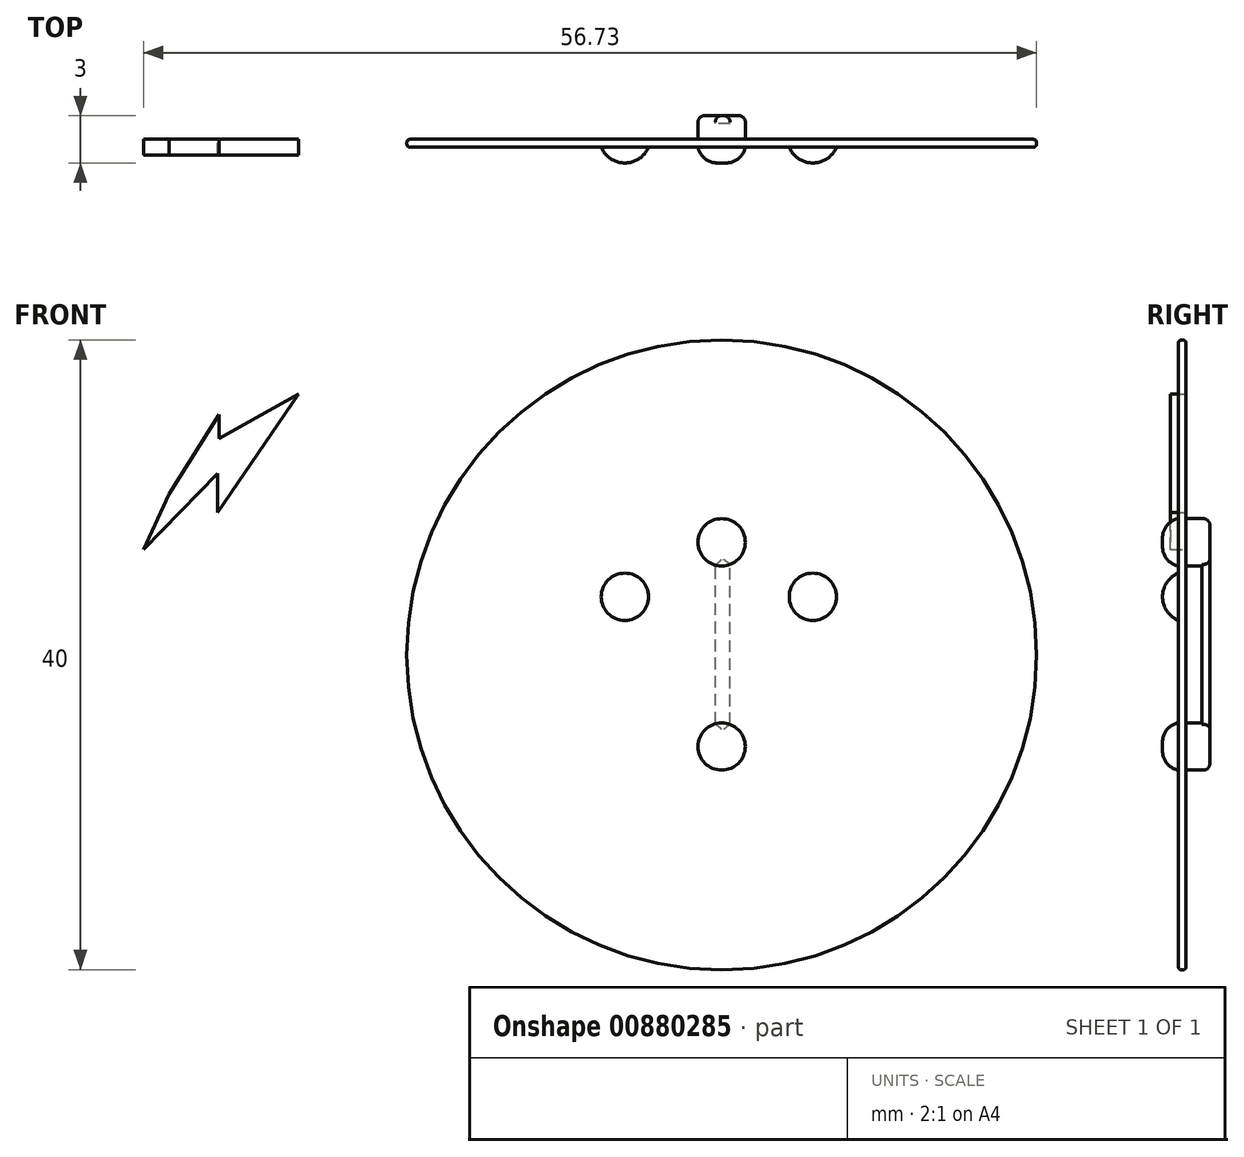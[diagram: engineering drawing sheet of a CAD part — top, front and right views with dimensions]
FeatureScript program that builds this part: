
annotation { "Feature Type Name" : "Feature", "Feature Type Description" : "" }
export const myFeature = defineFeature(function(context is Context, id is Id, definition is map)
    precondition{}
    {
        {
            var Q0;
            Q0=qCreatedBy(makeId("Front.planeOp"),FACE);
            var sketch = newSketch(context, id + "F0", { "sketchPlane" : qUnion([Q0])});
            skCircle(sketch, "E0", {"center": v(0, 0) * mm, "radius": 20 * mm});
            skSolve(sketch);
        }
        {
            var Q0;
            Q0=makeQuery(id+"F0.imprint","IMPRINT",FACE,{"disambiguationData":[TD([[makeQuery(id+"F0.imprint","IMPRINT",EDGE,{"derivedFrom":sQuery(id+"F0.wireOp",EDGE,"E0")}),1.0]])]});
            extrude(context, id + "F1", {"entities" : qUnion([Q0]), "depth" : .5 * mm, "offsetDistance" : 25 * mm});
        }
        {
            var Q0;
            Q0=makeQuery(id+"F1.opExtrude","CAP_FACE",FACE,{"disambiguationData":[OSD([sQuery(id+"F0.wireOp",EDGE,"E0")])],"isStart":true});
            var Q1;
            Q1=makeQuery(id+"F1.opExtrude","CAP_EDGE",EDGE,{"disambiguationData":[OSD([sQuery(id+"F0.wireOp",EDGE,"E0")])],"isStart":true});
            var Q2;
            Q2=makeQuery(id+"F1.opExtrude","CAP_EDGE",EDGE,{"disambiguationData":[OSD([sQuery(id+"F0.wireOp",EDGE,"E0")])],"isStart":false});
            var Q3;
            Q3=makeQuery(id+"F1.opExtrude","CAP_FACE",FACE,{"disambiguationData":[OSD([sQuery(id+"F0.wireOp",EDGE,"E0")])],"isStart":false});
            fillet(context, id + "F2", {"entities" : qUnion([Q0, Q1, Q2, Q3]), "radius" : .2 * mm, "tangentPropagation" : true, "allowEdgeOverflow" : false});
        }
        {
            var Q0;
            Q0=qCreatedBy(makeId("Front.planeOp"),FACE);
            var sketch = newSketch(context, id + "F3", { "sketchPlane" : qUnion([Q0])});
            skCircle(sketch, "E1", {"center": v(0, 7.16) * mm, "radius": 1.5 * mm});
            skCircle(sketch, "E2", {"center": v(0, -5.82) * mm, "radius": 1.5 * mm});
            skSolve(sketch);
        }
        {
            var Q0;
            Q0=makeQuery(id+"F3.imprint","IMPRINT",FACE,{"disambiguationData":[TD([[makeQuery(id+"F3.imprint","IMPRINT",EDGE,{"derivedFrom":sQuery(id+"F3.wireOp",EDGE,"E2")}),1.0]])]});
            var Q1;
            Q1=makeQuery(id+"F3.imprint","IMPRINT",FACE,{"disambiguationData":[TD([[makeQuery(id+"F3.imprint","IMPRINT",EDGE,{"derivedFrom":sQuery(id+"F3.wireOp",EDGE,"E1")}),1.0]])]});
            extrude(context, id + "F4", {"entities" : qUnion([Q0, Q1]), "operationType" : NewBodyOperationType.ADD, "depth" : 1.5 * mm, "offsetDistance" : 25 * mm, "hasSecondDirection" : true, "secondDirectionOppositeDirection" : true, "secondDirectionDepth" : 1.5 * mm});
        }
        {
            var Q0;
            Q0=makeQuery(id+"F4.opExtrude","CAP_FACE",FACE,{"disambiguationData":[OSD([sQuery(id+"F3.wireOp",EDGE,"E2")])],"isStart":false});
            var Q1;
            Q1=makeQuery(id+"F4.opExtrude","CAP_FACE",FACE,{"disambiguationData":[OSD([sQuery(id+"F3.wireOp",EDGE,"E1")])],"isStart":false});
            fillet(context, id + "F5", {"entities" : qUnion([Q0, Q1]), "radius" : 1.23 * mm, "tangentPropagation" : true, "allowEdgeOverflow" : false});
        }
        {
            var Q0;
            Q0=makeQuery(id+"F4.opExtrude","CAP_FACE",FACE,{"disambiguationData":[OSD([sQuery(id+"F3.wireOp",EDGE,"E1")])],"isStart":true});
            var sketch = newSketch(context, id + "F6", { "sketchPlane" : qUnion([Q0])});
            skLineSegment(sketch, "E3.bottom", {"start": v(-0.54, -5.9) * mm, "end": v(0.4, -5.9) * mm});
            skLineSegment(sketch, "E3.top", {"start": v(-0.54, 7.33) * mm, "end": v(0.4, 7.33) * mm});
            skLineSegment(sketch, "E3.left", {"start": v(-0.54, -5.9) * mm, "end": v(-0.54, 7.33) * mm});
            skLineSegment(sketch, "E3.right", {"start": v(0.4, -5.9) * mm, "end": v(0.4, 7.33) * mm});
            skSolve(sketch);
        }
        {
            var Q0;
            {var subQ0=sQuery(id+"F6.wireOp",EDGE,"E3.bottom");Q0=makeQuery(id+"F6.imprint","IMPRINT",FACE,{"disambiguationData":[TD([[makeQuery(id+"F6.imprint","IMPRINT",EDGE,{"derivedFrom":subQ0}),1.0]])]});}
            var Q1;
            {var subQ0=sQuery(id+"F6.wireOp",EDGE,"E3.top");Q1=makeQuery(id+"F6.imprint","IMPRINT",FACE,{"disambiguationData":[TD([[makeQuery(id+"F6.imprint","IMPRINT",EDGE,{"derivedFrom":subQ0}),-1.0]])]});}
            extrude(context, id + "F7", {"entities" : qUnion([Q0, Q1]), "operationType" : NewBodyOperationType.ADD, "oppositeDirection" : true, "depth" : .5 * mm, "offsetDistance" : 25 * mm});
        }
        {
            var Q0;
            Q0=makeQuery(id+"F4.opExtrude","CAP_EDGE",EDGE,{"disambiguationData":[OSD([sQuery(id+"F3.wireOp",EDGE,"E1")])],"isStart":true});
            var Q1;
            Q1=makeQuery(id+"F7.opExtrude","CAP_EDGE",EDGE,{"disambiguationData":[OSD([sQuery(id+"F6.wireOp",EDGE,"E3.left")])],"isStart":true});
            var Q2;
            Q2=makeQuery(id+"F7.opExtrude","CAP_EDGE",EDGE,{"disambiguationData":[OSD([sQuery(id+"F6.wireOp",EDGE,"E3.right")])],"isStart":true});
            var Q3;
            Q3=makeQuery(id+"F7.boolean.opBoolean","MERGE",FACE,{"derivedFrom":[makeQuery(id+"F4.opExtrude","CAP_FACE",FACE,{"disambiguationData":[OSD([sQuery(id+"F3.wireOp",EDGE,"E1")])],"isStart":true}),makeQuery(id+"F4.opExtrude","CAP_FACE",FACE,{"disambiguationData":[OSD([sQuery(id+"F3.wireOp",EDGE,"E2")])],"isStart":true}),makeQuery(id+"F7.opExtrude","CAP_FACE",FACE,{"disambiguationData":[OSD([sQuery(id+"F6.wireOp",EDGE,"E3.bottom"),sQuery(id+"F6.wireOp",EDGE,"E3.top"),sQuery(id+"F6.wireOp",EDGE,"E3.left"),sQuery(id+"F6.wireOp",EDGE,"E3.right")])],"isStart":true})]});
            fillet(context, id + "F8", {"entities" : qUnion([Q0, Q1, Q2, Q3]), "radius" : .4 * mm, "tangentPropagation" : true, "allowEdgeOverflow" : false});
        }
        {
            var Q0;
            Q0=qCreatedBy(makeId("Front.planeOp"),FACE);
            var sketch = newSketch(context, id + "F9", { "sketchPlane" : qUnion([Q0])});
            skCircle(sketch, "E4", {"center": v(-6.15, 3.7) * mm, "radius": 1.5 * mm});
            skCircle(sketch, "E5", {"center": v(5.79, 3.7) * mm, "radius": 1.5 * mm});
            skSolve(sketch);
        }
        {
            var Q0;
            Q0=makeQuery(id+"F9.imprint","IMPRINT",FACE,{"disambiguationData":[TD([[makeQuery(id+"F9.imprint","IMPRINT",EDGE,{"derivedFrom":sQuery(id+"F9.wireOp",EDGE,"E4")}),1.0]])]});
            var Q1;
            Q1=makeQuery(id+"F9.imprint","IMPRINT",FACE,{"disambiguationData":[TD([[makeQuery(id+"F9.imprint","IMPRINT",EDGE,{"derivedFrom":sQuery(id+"F9.wireOp",EDGE,"E5")}),1.0]])]});
            extrude(context, id + "F10", {"entities" : qUnion([Q0, Q1]), "operationType" : NewBodyOperationType.ADD, "depth" : 1.5 * mm, "offsetDistance" : 25 * mm});
        }
        {
            var Q0;
            Q0=makeQuery(id+"F10.opExtrude","CAP_FACE",FACE,{"disambiguationData":[OSD([sQuery(id+"F9.wireOp",EDGE,"E4")])],"isStart":false});
            var Q1;
            Q1=makeQuery(id+"F10.opExtrude","CAP_FACE",FACE,{"disambiguationData":[OSD([sQuery(id+"F9.wireOp",EDGE,"E5")])],"isStart":false});
            fillet(context, id + "F11", {"entities" : qUnion([Q0, Q1]), "radius" : 1.6 * mm, "tangentPropagation" : true, "allowEdgeOverflow" : false});
        }
        {
            var Q0;
            Q0=qCreatedBy(makeId("Front.planeOp"),FACE);
            var sketch = newSketch(context, id + "F12", { "sketchPlane" : qUnion([Q0])});
            skLineSegment(sketch, "E6", {"start": v(-35.08, 10.22) * mm, "end": v(-36.73, 6.7) * mm});
            skLineSegment(sketch, "E7", {"start": v(-36.73, 6.7) * mm, "end": v(-32.03, 11.52) * mm});
            skLineSegment(sketch, "E8", {"start": v(-32.03, 11.52) * mm, "end": v(-32.03, 9.05) * mm});
            skLineSegment(sketch, "E9", {"start": v(-32.03, 9.05) * mm, "end": v(-26.87, 16.56) * mm});
            skLineSegment(sketch, "E10", {"start": v(-26.87, 16.56) * mm, "end": v(-31.91, 13.75) * mm});
            skLineSegment(sketch, "E11", {"start": v(-31.91, 13.75) * mm, "end": v(-31.91, 15.27) * mm});
            skLineSegment(sketch, "E12", {"start": v(-31.91, 15.27) * mm, "end": v(-35.08, 10.22) * mm});
            skSolve(sketch);
        }
        {
            var Q0;
            Q0=makeQuery(id+"F12.imprint","IMPRINT",FACE,{"disambiguationData":[TD([[makeQuery(id+"F12.imprint","IMPRINT",EDGE,{"derivedFrom":sQuery(id+"F12.wireOp",EDGE,"E6")}),1.0]])]});
            extrude(context, id + "F13", {"entities" : qUnion([Q0]), "depth" : 1 * mm, "offsetDistance" : 25 * mm});
        }
    });
